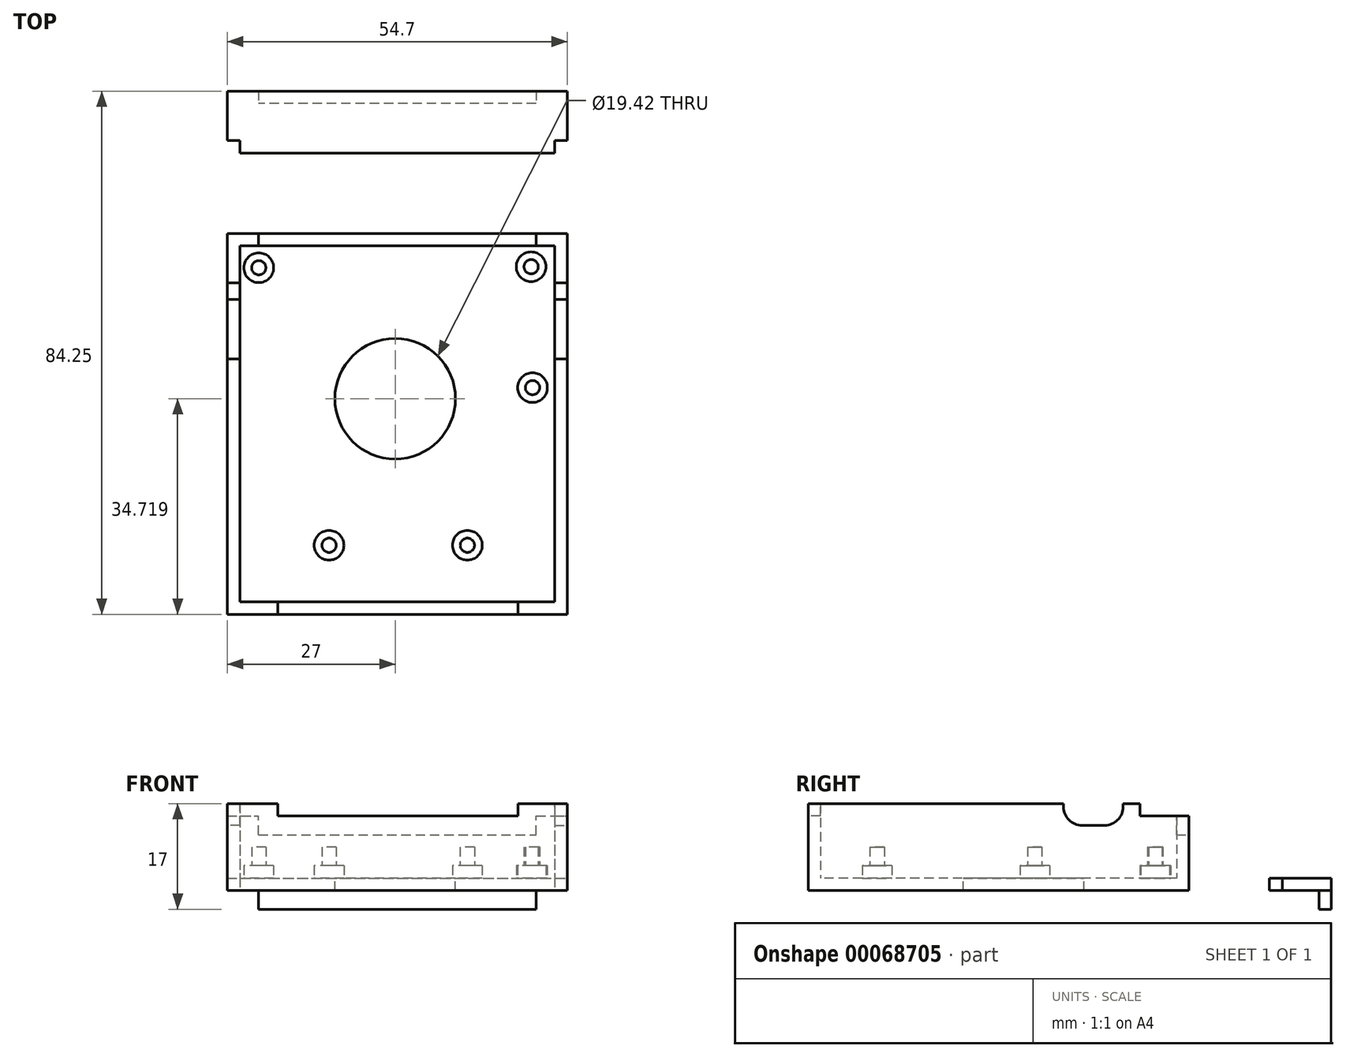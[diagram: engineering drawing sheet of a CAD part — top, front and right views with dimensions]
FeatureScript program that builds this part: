
annotation { "Feature Type Name" : "Feature", "Feature Type Description" : "" }
export const myFeature = defineFeature(function(context is Context, id is Id, definition is map)
    precondition{}
    {
        {
            var Q0;
            Q0=qCreatedBy(makeId("Top.planeOp"),FACE);
            var sketch = newSketch(context, id + "F0", { "sketchPlane" : qUnion([Q0])});
            skLineSegment(sketch, "E0.bottom", {"start": v(-25, 20) * mm, "end": v(25.7, 20) * mm});
            skLineSegment(sketch, "E0.top", {"start": v(-25, -37.32) * mm, "end": v(25.7, -37.32) * mm});
            skLineSegment(sketch, "E0.left", {"start": v(-25, 20) * mm, "end": v(-25, -37.32) * mm});
            skLineSegment(sketch, "E0.right", {"start": v(25.7, 20) * mm, "end": v(25.7, -37.32) * mm});
            skLineSegment(sketch, "E1.bottom", {"start": v(-27, 22) * mm, "end": v(27.7, 22) * mm});
            skLineSegment(sketch, "E1.top", {"start": v(-27, -39.32) * mm, "end": v(27.7, -39.32) * mm});
            skLineSegment(sketch, "E1.left", {"start": v(-27, 22) * mm, "end": v(-27, -39.32) * mm});
            skLineSegment(sketch, "E1.right", {"start": v(27.7, 22) * mm, "end": v(27.7, -39.32) * mm});
            skSolve(sketch);
        }
        {
            var Q0;
            Q0 = qSketchRegion(id + "F0", true);
            extrude(context, id + "F1", {"entities" : qUnion([Q0]), "depth" : 14 * mm});
        }
        {
            var Q0;
            Q0=makeQuery(id+"F0.imprint","IMPRINT",FACE,{"disambiguationData":[TD([[makeQuery(id+"F0.imprint","IMPRINT",EDGE,{"derivedFrom":sQuery(id+"F0.wireOp",EDGE,"E0.bottom")}),-1.0]])]});
            extrude(context, id + "F2", {"entities" : qUnion([Q0]), "operationType" : NewBodyOperationType.ADD, "depth" : 2 * mm});
        }
        {
            var Q0;
            Q0=makeQuery(id+"F2.opExtrude","CAP_FACE",FACE,{"disambiguationData":[OSD([sQuery(id+"F0.wireOp",EDGE,"E0.bottom"),sQuery(id+"F0.wireOp",EDGE,"E0.top"),sQuery(id+"F0.wireOp",EDGE,"E0.left"),sQuery(id+"F0.wireOp",EDGE,"E0.right")])],"isStart":false});
            var sketch = newSketch(context, id + "F3", { "sketchPlane" : qUnion([Q0])});
            skCircle(sketch, "E2", {"center": v(21.9, 16.65) * mm, "radius": 1.15 * mm});
            skCircle(sketch, "E3", {"center": v(-21.97, 16.5) * mm, "radius": 1.15 * mm});
            skCircle(sketch, "E4", {"center": v(22.11, -2.82) * mm, "radius": 1.15 * mm});
            skCircle(sketch, "E5", {"center": v(11.62, -28.2) * mm, "radius": 1.15 * mm});
            skCircle(sketch, "E6", {"center": v(-10.65, -28.2) * mm, "radius": 1.15 * mm});
            skSolve(sketch);
        }
        {
            var Q0;
            Q0 = qSketchRegion(id + "F3", true);
            extrude(context, id + "F4", {"entities" : qUnion([Q0]), "operationType" : NewBodyOperationType.ADD, "depth" : 5 * mm});
        }
        {
            var Q0;
            Q0=makeQuery(id+"F2.opExtrude","CAP_FACE",FACE,{"disambiguationData":[OSD([sQuery(id+"F0.wireOp",EDGE,"E0.bottom"),sQuery(id+"F0.wireOp",EDGE,"E0.top"),sQuery(id+"F0.wireOp",EDGE,"E0.left"),sQuery(id+"F0.wireOp",EDGE,"E0.right")])],"isStart":false});
            var sketch = newSketch(context, id + "F5", { "sketchPlane" : qUnion([Q0])});
            skCircle(sketch, "E7", {"center": v(-10.65, -28.2) * mm, "radius": 2.4 * mm});
            skCircle(sketch, "E8", {"center": v(11.62, -28.2) * mm, "radius": 2.4 * mm});
            skCircle(sketch, "E9", {"center": v(22.11, -2.82) * mm, "radius": 2.4 * mm});
            skCircle(sketch, "E10", {"center": v(21.9, 16.65) * mm, "radius": 2.4 * mm});
            skCircle(sketch, "E11", {"center": v(-21.97, 16.5) * mm, "radius": 2.4 * mm});
            skSolve(sketch);
        }
        {
            var Q0;
            Q0 = qSketchRegion(id + "F5", true);
            extrude(context, id + "F6", {"entities" : qUnion([Q0]), "operationType" : NewBodyOperationType.ADD, "depth" : 2 * mm});
        }
        {
            var Q0;
            Q0=makeQuery(id+"F1.opExtrude","CAP_FACE",FACE,{"disambiguationData":[OSD([sQuery(id+"F0.wireOp",EDGE,"E0.bottom"),sQuery(id+"F0.wireOp",EDGE,"E0.top"),sQuery(id+"F0.wireOp",EDGE,"E0.left"),sQuery(id+"F0.wireOp",EDGE,"E0.right"),sQuery(id+"F0.wireOp",EDGE,"E1.bottom"),sQuery(id+"F0.wireOp",EDGE,"E1.top"),sQuery(id+"F0.wireOp",EDGE,"E1.left"),sQuery(id+"F0.wireOp",EDGE,"E1.right")])],"isStart":false});
            var sketch = newSketch(context, id + "F7", { "sketchPlane" : qUnion([Q0])});
            skLineSegment(sketch, "E12.bottom", {"start": v(25.7, 1.8) * mm, "end": v(27.7, 1.8) * mm});
            skLineSegment(sketch, "E12.top", {"start": v(25.7, 11.4) * mm, "end": v(27.7, 11.4) * mm});
            skLineSegment(sketch, "E12.left", {"start": v(25.7, 1.8) * mm, "end": v(25.7, 11.4) * mm});
            skLineSegment(sketch, "E12.right", {"start": v(27.7, 1.8) * mm, "end": v(27.7, 11.4) * mm});
            skSolve(sketch);
        }
        {
            var Q0;
            Q0 = qSketchRegion(id + "F7", true);
            extrude(context, id + "F8", {"entities" : qUnion([Q0]), "operationType" : NewBodyOperationType.REMOVE, "oppositeDirection" : true, "depth" : 3.5 * mm});
        }
        {
            var Q0;
            Q0=makeQuery(id+"F8.boolean.opBoolean","COPY",EDGE,{"derivedFrom":makeQuery(id+"F8.opExtrude","CAP_EDGE",EDGE,{"disambiguationData":[OSD([sQuery(id+"F7.wireOp",EDGE,"E12.top")])],"isStart":false})});
            var Q1;
            Q1=makeQuery(id+"F8.boolean.opBoolean","COPY",EDGE,{"derivedFrom":makeQuery(id+"F8.opExtrude","CAP_EDGE",EDGE,{"disambiguationData":[OSD([sQuery(id+"F7.wireOp",EDGE,"E12.bottom")])],"isStart":false})});
            fillet(context, id + "F9", {"entities" : qUnion([Q0, Q1]), "radius" : 3 * mm, "tangentPropagation" : true, "allowEdgeOverflow" : false});
        }
        {
            var Q0;
            Q0=makeQuery(id+"F1.opExtrude","CAP_FACE",FACE,{"disambiguationData":[OSD([sQuery(id+"F0.wireOp",EDGE,"E0.bottom"),sQuery(id+"F0.wireOp",EDGE,"E0.top"),sQuery(id+"F0.wireOp",EDGE,"E0.left"),sQuery(id+"F0.wireOp",EDGE,"E0.right"),sQuery(id+"F0.wireOp",EDGE,"E1.bottom"),sQuery(id+"F0.wireOp",EDGE,"E1.top"),sQuery(id+"F0.wireOp",EDGE,"E1.left"),sQuery(id+"F0.wireOp",EDGE,"E1.right")])],"isStart":false});
            var sketch = newSketch(context, id + "F10", { "sketchPlane" : qUnion([Q0])});
            skLineSegment(sketch, "E13.bottom", {"start": v(-25, 11.4) * mm, "end": v(-27, 11.4) * mm});
            skLineSegment(sketch, "E13.top", {"start": v(-25, 1.8) * mm, "end": v(-27, 1.8) * mm});
            skLineSegment(sketch, "E13.left", {"start": v(-25, 11.4) * mm, "end": v(-25, 1.8) * mm});
            skLineSegment(sketch, "E13.right", {"start": v(-27, 11.4) * mm, "end": v(-27, 1.8) * mm});
            skSolve(sketch);
        }
        {
            var Q0;
            Q0 = qSketchRegion(id + "F10", true);
            extrude(context, id + "F11", {"entities" : qUnion([Q0]), "operationType" : NewBodyOperationType.REMOVE, "oppositeDirection" : true, "depth" : 3.5 * mm});
        }
        {
            var Q0;
            Q0=makeQuery(id+"F11.boolean.opBoolean","COPY",EDGE,{"derivedFrom":makeQuery(id+"F11.opExtrude","CAP_EDGE",EDGE,{"disambiguationData":[OSD([sQuery(id+"F10.wireOp",EDGE,"E13.bottom")])],"isStart":false})});
            var Q1;
            Q1=makeQuery(id+"F11.boolean.opBoolean","COPY",EDGE,{"derivedFrom":makeQuery(id+"F11.opExtrude","CAP_EDGE",EDGE,{"disambiguationData":[OSD([sQuery(id+"F10.wireOp",EDGE,"E13.top")])],"isStart":false})});
            fillet(context, id + "F12", {"entities" : qUnion([Q0, Q1]), "radius" : 3 * mm, "tangentPropagation" : true, "allowEdgeOverflow" : false});
        }
        {
            var Q0;
            {var subQ0=sQuery(id+"F0.wireOp",EDGE,"E1.top");var subQ1=sQuery(id+"F0.wireOp",EDGE,"E0.right");var subQ2=sQuery(id+"F0.wireOp",EDGE,"E0.left");var subQ3=sQuery(id+"F0.wireOp",EDGE,"E0.top");var subQ4=sQuery(id+"F0.wireOp",EDGE,"E1.left");var subQ5=sQuery(id+"F0.wireOp",EDGE,"E1.right");Q0=makeQuery(id+"F11.boolean.opBoolean","SPLIT",FACE,{"disambiguationData":[TD([makeQuery(id+"F1.opExtrude","SWEPT_FACE",FACE,{"disambiguationData":[OSD([subQ3])]})])],"derivedFrom":makeQuery(id+"F1.opExtrude","CAP_FACE",FACE,{"disambiguationData":[OSD([sQuery(id+"F0.wireOp",EDGE,"E0.bottom"),subQ3,subQ2,subQ1,sQuery(id+"F0.wireOp",EDGE,"E1.bottom"),subQ0,subQ4,subQ5])],"isStart":false})});}
            var sketch = newSketch(context, id + "F13", { "sketchPlane" : qUnion([Q0])});
            skLineSegment(sketch, "E14.bottom", {"start": v(-18.88, -37.32) * mm, "end": v(19.78, -37.32) * mm});
            skLineSegment(sketch, "E14.top", {"start": v(-18.88, -39.32) * mm, "end": v(19.78, -39.32) * mm});
            skLineSegment(sketch, "E14.left", {"start": v(-18.88, -37.32) * mm, "end": v(-18.88, -39.32) * mm});
            skLineSegment(sketch, "E14.right", {"start": v(19.78, -37.32) * mm, "end": v(19.78, -39.32) * mm});
            skSolve(sketch);
        }
        {
            var Q0;
            Q0 = qSketchRegion(id + "F13", true);
            extrude(context, id + "F14", {"entities" : qUnion([Q0]), "operationType" : NewBodyOperationType.REMOVE, "oppositeDirection" : true, "depth" : 2 * mm});
        }
        {
            var Q0;
            {var subQ0=sQuery(id+"F0.wireOp",EDGE,"E1.bottom");var subQ1=sQuery(id+"F0.wireOp",EDGE,"E0.right");var subQ2=sQuery(id+"F0.wireOp",EDGE,"E0.left");var subQ3=sQuery(id+"F0.wireOp",EDGE,"E0.bottom");var subQ4=sQuery(id+"F0.wireOp",EDGE,"E1.left");var subQ5=sQuery(id+"F0.wireOp",EDGE,"E1.right");Q0=makeQuery(id+"F11.boolean.opBoolean","SPLIT",FACE,{"disambiguationData":[TD([makeQuery(id+"F1.opExtrude","SWEPT_FACE",FACE,{"disambiguationData":[OSD([subQ3])]})])],"derivedFrom":makeQuery(id+"F1.opExtrude","CAP_FACE",FACE,{"disambiguationData":[OSD([subQ3,sQuery(id+"F0.wireOp",EDGE,"E0.top"),subQ2,subQ1,subQ0,sQuery(id+"F0.wireOp",EDGE,"E1.top"),subQ4,subQ5])],"isStart":false})});}
            var sketch = newSketch(context, id + "F15", { "sketchPlane" : qUnion([Q0])});
            skLineSegment(sketch, "E15.bottom", {"start": v(-27, 22) * mm, "end": v(27.7, 22) * mm});
            skLineSegment(sketch, "E15.top", {"start": v(-27, 14.09) * mm, "end": v(27.7, 14.09) * mm});
            skLineSegment(sketch, "E15.left", {"start": v(-27, 22) * mm, "end": v(-27, 14.09) * mm});
            skLineSegment(sketch, "E15.right", {"start": v(27.7, 22) * mm, "end": v(27.7, 14.09) * mm});
            skSolve(sketch);
        }
        {
            var Q0;
            Q0 = qSketchRegion(id + "F15", true);
            extrude(context, id + "F16", {"entities" : qUnion([Q0]), "operationType" : NewBodyOperationType.REMOVE, "oppositeDirection" : true, "depth" : 2 * mm});
        }
        {
            var Q0;
            Q0=qCreatedBy(makeId("Top.planeOp"),FACE);
            var sketch = newSketch(context, id + "F17", { "sketchPlane" : qUnion([Q0])});
            skLineSegment(sketch, "E16.bottom", {"start": v(-27, 44.93) * mm, "end": v(27.7, 44.93) * mm});
            skLineSegment(sketch, "E16.top", {"start": v(-27, 37.01) * mm, "end": v(27.7, 37.01) * mm});
            skLineSegment(sketch, "E16.left", {"start": v(-27, 44.93) * mm, "end": v(-27, 37.01) * mm});
            skLineSegment(sketch, "E16.right", {"start": v(27.7, 44.93) * mm, "end": v(27.7, 37.01) * mm});
            skLineSegment(sketch, "E17.bottom", {"start": v(-25, 37.01) * mm, "end": v(25.7, 37.01) * mm});
            skLineSegment(sketch, "E17.top", {"start": v(-25, 34.96) * mm, "end": v(25.7, 34.96) * mm});
            skLineSegment(sketch, "E17.left", {"start": v(-25, 37.01) * mm, "end": v(-25, 34.96) * mm});
            skLineSegment(sketch, "E17.right", {"start": v(25.7, 37.01) * mm, "end": v(25.7, 34.96) * mm});
            skSolve(sketch);
        }
        {
            var Q0;
            Q0 = qSketchRegion(id + "F17", true);
            extrude(context, id + "F18", {"entities" : qUnion([Q0]), "depth" : 2 * mm});
        }
        {
            var Q0;
            Q0=makeQuery(id+"F18.opExtrude","CAP_FACE",FACE,{"disambiguationData":[OSD([sQuery(id+"F17.wireOp",EDGE,"E16.bottom"),sQuery(id+"F17.wireOp",EDGE,"E16.top"),sQuery(id+"F17.wireOp",EDGE,"E16.left"),sQuery(id+"F17.wireOp",EDGE,"E16.right"),sQuery(id+"F17.wireOp",EDGE,"E17.top"),sQuery(id+"F17.wireOp",EDGE,"E17.left"),sQuery(id+"F17.wireOp",EDGE,"E17.right")])],"isStart":true});
            var sketch = newSketch(context, id + "F19", { "sketchPlane" : qUnion([Q0])});
            skLineSegment(sketch, "E18.bottom", {"start": v(22.7, -44.93) * mm, "end": v(-22, -44.93) * mm});
            skLineSegment(sketch, "E18.top", {"start": v(22.7, -42.93) * mm, "end": v(-22, -42.93) * mm});
            skLineSegment(sketch, "E18.left", {"start": v(22.7, -44.93) * mm, "end": v(22.7, -42.93) * mm});
            skLineSegment(sketch, "E18.right", {"start": v(-22, -44.93) * mm, "end": v(-22, -42.93) * mm});
            skSolve(sketch);
        }
        {
            var Q0;
            Q0=makeQuery(id+"F19.imprint","IMPRINT",FACE,{"disambiguationData":[TD([[makeQuery(id+"F19.imprint","IMPRINT",EDGE,{"derivedFrom":sQuery(id+"F19.wireOp",EDGE,"E18.bottom")}),1.0]])]});
            extrude(context, id + "F20", {"entities" : qUnion([Q0]), "operationType" : NewBodyOperationType.ADD, "depth" : 3 * mm});
        }
        {
            var Q0;
            Q0=makeQuery(id+"F16.boolean.opBoolean","COPY",FACE,{"derivedFrom":makeQuery(id+"F16.opExtrude","CAP_FACE",FACE,{"disambiguationData":[OSD([sQuery(id+"F15.wireOp",EDGE,"E15.bottom"),sQuery(id+"F15.wireOp",EDGE,"E15.top"),sQuery(id+"F15.wireOp",EDGE,"E15.left"),sQuery(id+"F15.wireOp",EDGE,"E15.right")])],"isStart":false})});
            var sketch = newSketch(context, id + "F21", { "sketchPlane" : qUnion([Q0])});
            skLineSegment(sketch, "E19.bottom", {"start": v(22.7, 20) * mm, "end": v(-22, 20) * mm});
            skLineSegment(sketch, "E19.top", {"start": v(22.7, 22) * mm, "end": v(-22, 22) * mm});
            skLineSegment(sketch, "E19.left", {"start": v(22.7, 20) * mm, "end": v(22.7, 22) * mm});
            skLineSegment(sketch, "E19.right", {"start": v(-22, 20) * mm, "end": v(-22, 22) * mm});
            skSolve(sketch);
        }
        {
            var Q0;
            Q0=makeQuery(id+"F21.imprint","IMPRINT",FACE,{"disambiguationData":[TD([[makeQuery(id+"F21.imprint","IMPRINT",EDGE,{"derivedFrom":sQuery(id+"F21.wireOp",EDGE,"E19.bottom")}),1.0]])]});
            extrude(context, id + "F22", {"entities" : qUnion([Q0]), "operationType" : NewBodyOperationType.REMOVE, "oppositeDirection" : true, "depth" : 3 * mm});
        }
        {
            var Q0;
            Q0=makeQuery(id+"F2.opExtrude","CAP_FACE",FACE,{"disambiguationData":[OSD([sQuery(id+"F0.wireOp",EDGE,"E0.bottom"),sQuery(id+"F0.wireOp",EDGE,"E0.top"),sQuery(id+"F0.wireOp",EDGE,"E0.left"),sQuery(id+"F0.wireOp",EDGE,"E0.right")])],"isStart":false});
            var sketch = newSketch(context, id + "F23", { "sketchPlane" : qUnion([Q0])});
            skCircle(sketch, "E20", {"center": v(0, -4.6) * mm, "radius": 9.7 * mm});
            skSolve(sketch);
        }
        {
            var Q0;
            Q0=makeQuery(id+"F23.imprint","IMPRINT",FACE,{"disambiguationData":[TD([[makeQuery(id+"F23.imprint","IMPRINT",EDGE,{"derivedFrom":sQuery(id+"F23.wireOp",EDGE,"E20")}),1.0]])]});
            extrude(context, id + "F24", {"entities" : qUnion([Q0]), "operationType" : NewBodyOperationType.REMOVE, "oppositeDirection" : true, "depth" : 3 * mm});
        }
    });
